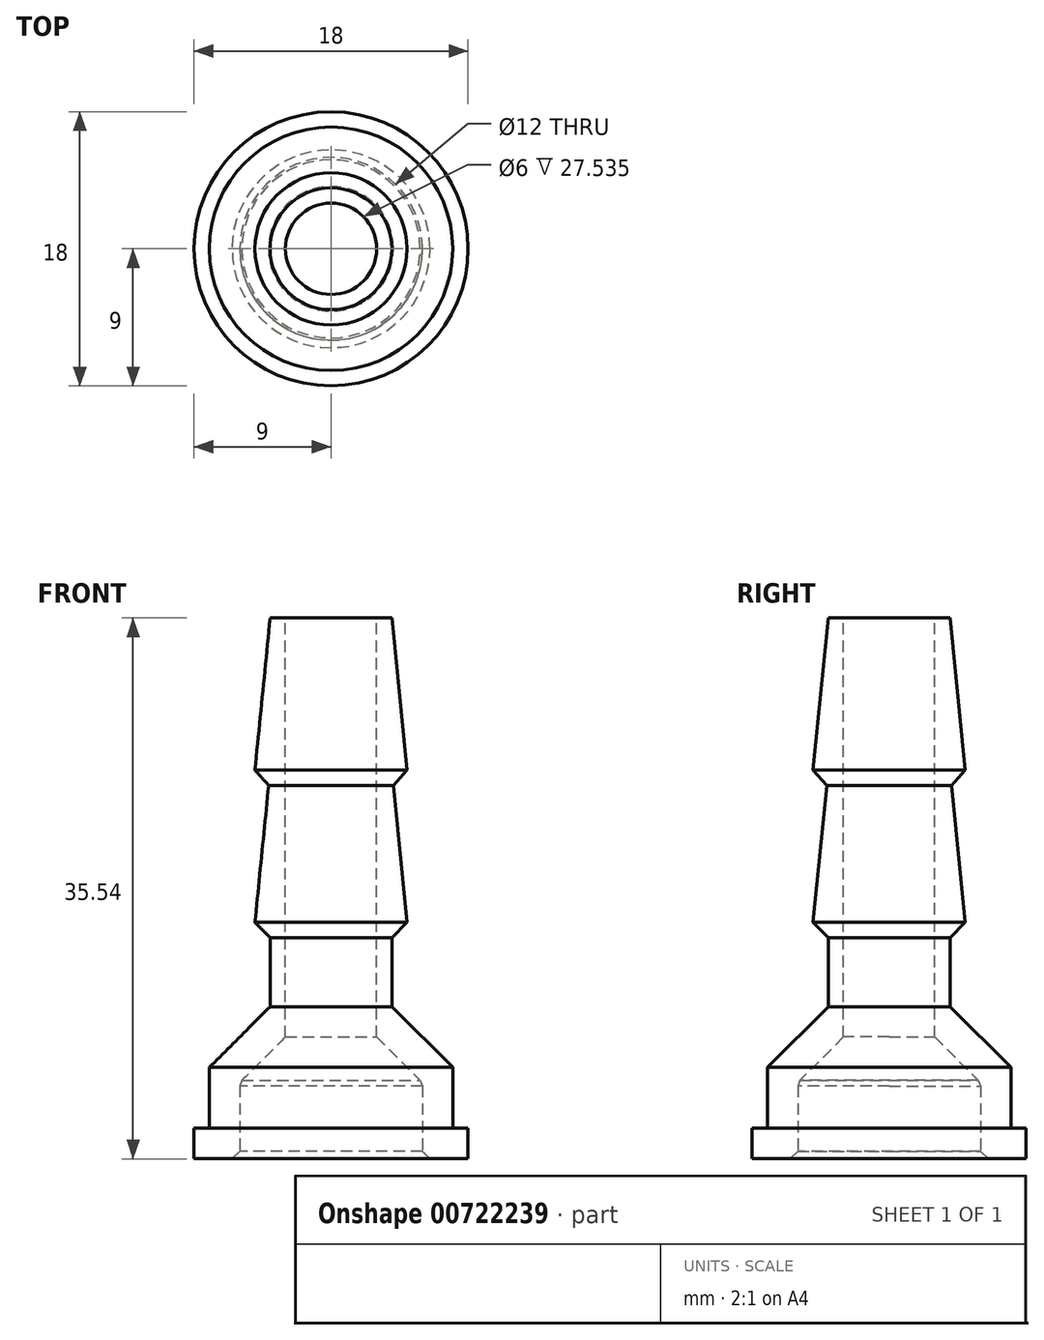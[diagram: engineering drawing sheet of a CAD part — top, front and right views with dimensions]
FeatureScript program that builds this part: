
annotation { "Feature Type Name" : "Feature", "Feature Type Description" : "" }
export const myFeature = defineFeature(function(context is Context, id is Id, definition is map)
    precondition{}
    {
        {
            var Q0;
            Q0=qCreatedBy(makeId("Front.planeOp"),FACE);
            var sketch = newSketch(context, id + "F0", { "sketchPlane" : qUnion([Q0])});
            skLineSegment(sketch, "E0", {"start": v(0, 0.46) * mm, "end": v(0, 25) * mm});
            skLineSegment(sketch, "E1", {"start": v(0, 25) * mm, "end": v(-4, 25) * mm});
            skLineSegment(sketch, "E2", {"start": v(-4, 25) * mm, "end": v(-5, 15) * mm});
            skLineSegment(sketch, "E3", {"start": v(-4.1, 14) * mm, "end": v(-5, 5) * mm});
            skPoint(sketch, "E4.orphan", {"position": v(0, 15) * mm});
            skLineSegment(sketch, "E5", {"start": v(-6, -10.54) * mm, "end": v(-6, -5.54) * mm});
            skLineSegment(sketch, "E6", {"start": v(-8, -8.54) * mm, "end": v(-8, -4.54) * mm});
            skLineSegment(sketch, "E7", {"start": v(-4, -0.54) * mm, "end": v(-8, -4.54) * mm});
            skLineSegment(sketch, "E8", {"start": v(-8, -8.54) * mm, "end": v(-9, -8.54) * mm});
            skLineSegment(sketch, "E9", {"start": v(-9, -8.54) * mm, "end": v(-9, -10.54) * mm});
            skLineSegment(sketch, "E10", {"start": v(-9, -10.54) * mm, "end": v(-6, -10.54) * mm});
            skLineSegment(sketch, "E11", {"start": v(-4, 4) * mm, "end": v(-5, 5) * mm});
            skLineSegment(sketch, "E12", {"start": v(-4, 4) * mm, "end": v(-4, -0.54) * mm});
            skLineSegment(sketch, "E13", {"start": v(-6, -5.54) * mm, "end": v(0, 0.46) * mm});
            skLineSegment(sketch, "E14", {"start": v(-4.1, 14) * mm, "end": v(-5, 15) * mm});
            skSolve(sketch);
        }
        {
            var Q0;
            Q0=makeQuery(id+"F0.imprint","IMPRINT",FACE,{"disambiguationData":[TD([[makeQuery(id+"F0.imprint","IMPRINT",EDGE,{"derivedFrom":sQuery(id+"F0.wireOp",EDGE,"E0")}),1.0]])]});
            var Q1;
            Q1=sQuery(id+"F0.wireOp",EDGE,"E0");
            revolve(context, id + "F1", {"surfaceOperationType" : NewSurfaceOperationType.NEW, "entities" : qUnion([Q0]), "axis" : qUnion([Q1]), "revolveType" : RevolveType.FULL});
        }
        {
            var Q0;
            Q0=makeQuery(id+"F1.opRevolve","SWEPT_FACE",FACE,{"disambiguationData":[OSD([sQuery(id+"F0.wireOp",EDGE,"E1")])]});
            var sketch = newSketch(context, id + "F2", { "sketchPlane" : qUnion([Q0])});
            skCircle(sketch, "E15", {"center": v(0, 0) * mm, "radius": 3 * mm});
            skSolve(sketch);
        }
        {
            var Q0;
            Q0=makeQuery(id+"F2.imprint","IMPRINT",FACE,{"disambiguationData":[TD([[makeQuery(id+"F2.imprint","IMPRINT",EDGE,{"derivedFrom":sQuery(id+"F2.wireOp",EDGE,"E15")}),1.0]])]});
            extrude(context, id + "F3", {"entities" : qUnion([Q0]), "operationType" : NewBodyOperationType.REMOVE, "endBound" : BoundingType.THROUGH_ALL, "oppositeDirection" : true, "depth" : 25 * mm, "offsetDistance" : 25 * mm});
        }
        {
            var Q0;
            Q0=makeQuery(id+"F1.opRevolve","SWEPT_EDGE",EDGE,{"disambiguationData":[OSD([sQuery(id+"F0.wireOp",EDGE,"I5wHl5To-vDyZ-EEAD-0txk-vuxYSV94XfbA"),sQuery(id+"F0.wireOp",EDGE,"hUesTbg2-FTRX-jMIG-RKOx-UDQJ9JFYW7Gu")])]});
            var Q1;
            Q1=makeQuery(id+"F1.opRevolve","SWEPT_EDGE",EDGE,{"disambiguationData":[OSD([sQuery(id+"F0.wireOp",EDGE,"JJRLu1hI-lRfn-RYQr-SIdh-gOZYJzPz1OP0"),sQuery(id+"F0.wireOp",EDGE,"E5")])]});
            var Q2;
            Q2=makeQuery(id+"F3.boolean.opBoolean","INTERSECT",EDGE,{"derivedFrom":[makeQuery(id+"F1.opRevolve","SWEPT_FACE",FACE,{"disambiguationData":[OSD([sQuery(id+"F0.wireOp",EDGE,"pzMMuw05-dyJC-pGSs-Y9qg-YOac458GIloe")])]}),makeQuery(id+"F3.opExtrude","SWEPT_FACE",FACE,{"disambiguationData":[OSD([sQuery(id+"F2.wireOp",EDGE,"E15")])]})]});
            chamfer(context, id + "F4", {"entities" : qUnion([Q0, Q1, Q2]), "width" : .5 * mm, "tangentPropagation" : true});
        }
    });
